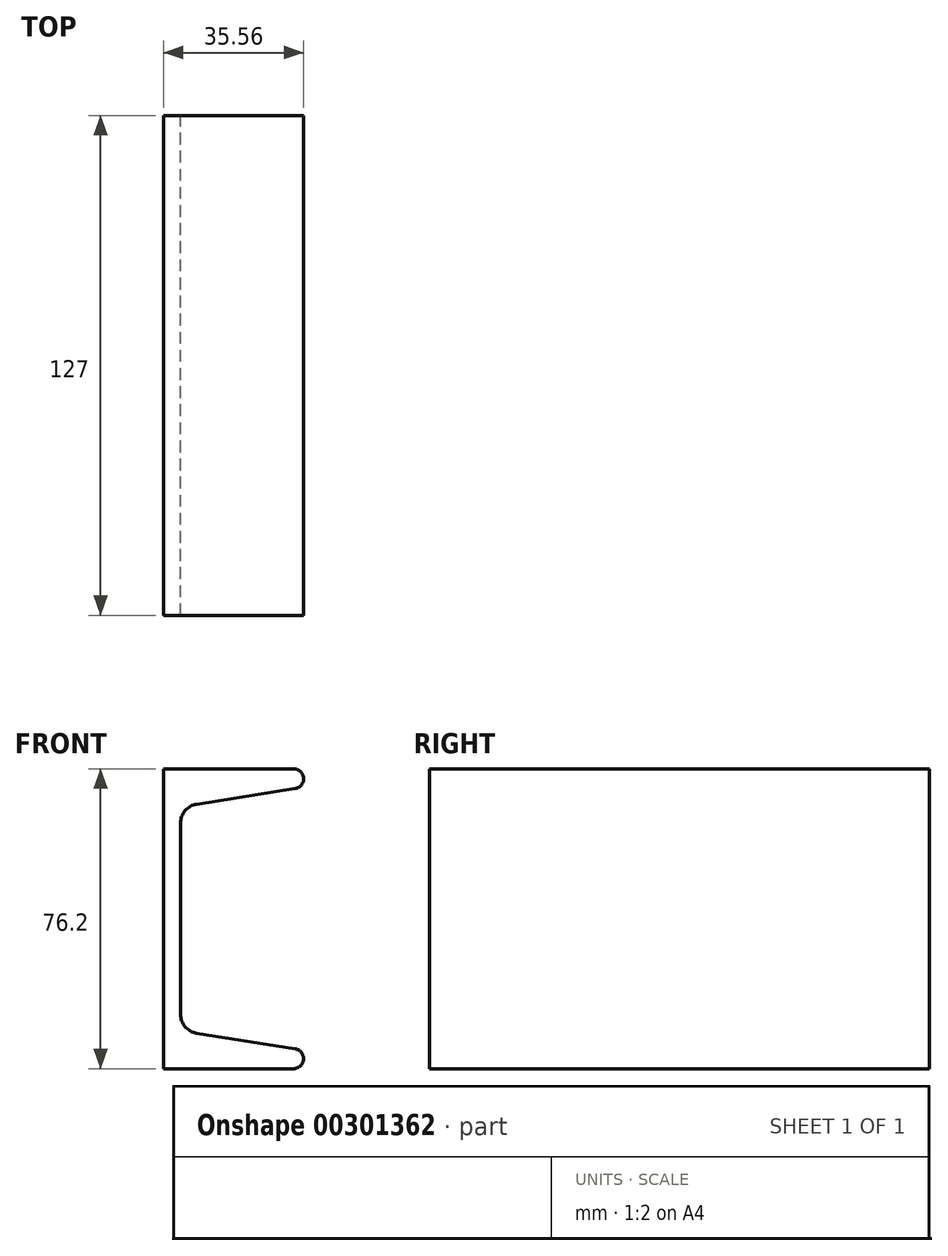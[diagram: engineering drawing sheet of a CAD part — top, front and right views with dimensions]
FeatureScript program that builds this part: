
annotation { "Feature Type Name" : "Feature", "Feature Type Description" : "" }
export const myFeature = defineFeature(function(context is Context, id is Id, definition is map)
    precondition{}
    {
        {
            var Q0;
            Q0=qCreatedBy(makeId("Front.planeOp"),FACE);
            var sketch = newSketch(context, id + "F0", { "sketchPlane" : qUnion([Q0])});
            skLineSegment(sketch, "E0", {"start": v(-59.3, 0) * mm, "end": v(-59.3, 38.1) * mm});
            skLineSegment(sketch, "E1", {"start": v(-59.3, 38.1) * mm, "end": v(-26.28, 38.1) * mm});
            skLineSegment(sketch, "E2", {"start": v(-25.88, 33.05) * mm, "end": v(-50.9, 29.1) * mm});
            skLineSegment(sketch, "E3", {"start": v(-54.98, 24.3) * mm, "end": v(-54.98, 0) * mm});
            skPoint(sketch, "E4.visualSharp", {"position": v(6, 38.1) * mm});
            skArc(sketch, "E4.filletArc", {"start": v(-25.88, 33.05) * mm, "mid": v(-23.75, 35.76) * mm, "end": v(-26.28, 38.1) * mm});
            skPoint(sketch, "E5.visualSharp", {"position": v(-54.98, 28.44) * mm});
            skArc(sketch, "E5.filletArc", {"start": v(-50.9, 29.1) * mm, "mid": v(-53.82, 27.45) * mm, "end": v(-54.98, 24.3) * mm});
            skArc(sketch, "E6.MirrorCS", {"start": v(-25.88, -33.05) * mm, "mid": v(-23.75, -35.76) * mm, "end": v(-26.28, -38.1) * mm});
            skArc(sketch, "E7.MirrorCS", {"start": v(-50.9, -29.1) * mm, "mid": v(-53.82, -27.45) * mm, "end": v(-54.98, -24.3) * mm});
            skPoint(sketch, "E8.MirrorP", {"position": v(6, -38.1) * mm});
            skPoint(sketch, "E9.MirrorP", {"position": v(-54.98, -28.44) * mm});
            skLineSegment(sketch, "E10.MirrorCS", {"start": v(-54.98, -24.3) * mm, "end": v(-54.98, 0) * mm});
            skLineSegment(sketch, "E11.MirrorCS", {"start": v(-59.3, -38.1) * mm, "end": v(-26.28, -38.1) * mm});
            skLineSegment(sketch, "E12.MirrorCS", {"start": v(-59.3, 0) * mm, "end": v(-59.3, -38.1) * mm});
            skLineSegment(sketch, "E13.MirrorCS", {"start": v(-25.88, -33.05) * mm, "end": v(-50.9, -29.1) * mm});
            skSolve(sketch);
        }
        {
            var Q0;
            Q0=makeQuery(id+"F0.imprint","IMPRINT",FACE,{"disambiguationData":[TD([[makeQuery(id+"F0.imprint","IMPRINT",EDGE,{"derivedFrom":sQuery(id+"F0.wireOp",EDGE,"E0")}),-1.0]])]});
            extrude(context, id + "F1", {"entities" : qUnion([Q0]), "depth" : 127 * mm});
        }
    });
